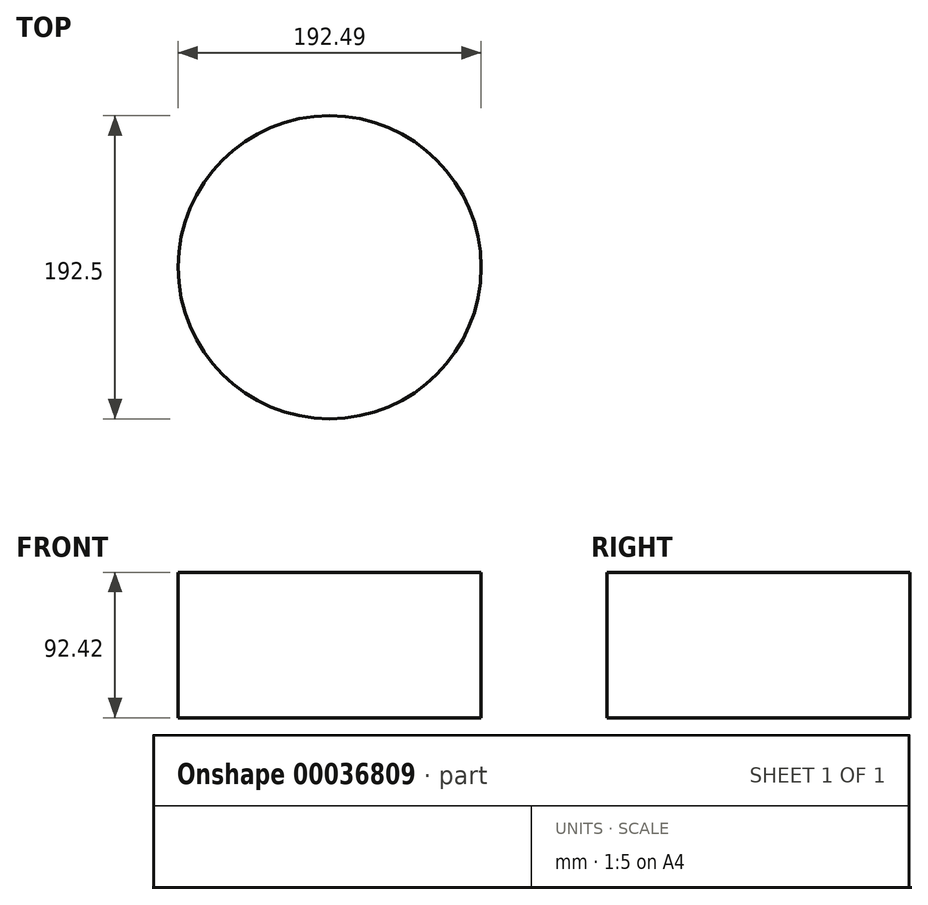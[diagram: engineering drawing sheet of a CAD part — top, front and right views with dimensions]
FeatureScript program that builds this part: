
annotation { "Feature Type Name" : "Feature", "Feature Type Description" : "" }
export const myFeature = defineFeature(function(context is Context, id is Id, definition is map)
    precondition{}
    {
        {
            var Q0;
            Q0=qCreatedBy(makeId("Top.planeOp"),FACE);
            var sketch = newSketch(context, id + "F0", { "sketchPlane" : qUnion([Q0])});
            skCircle(sketch, "E0", {"center": v(22.5, -47.04) * mm, "radius": 96.25 * mm});
            skSolve(sketch);
        }
        {
            var Q0;
            Q0=makeQuery(id+"F0.imprint","IMPRINT",FACE,{"disambiguationData":[TD([[makeQuery(id+"F0.imprint","IMPRINT",EDGE,{"derivedFrom":sQuery(id+"F0.wireOp",EDGE,"E0")}),1.0]])]});
            extrude(context, id + "F1", {"entities" : qUnion([Q0]), "depth" : 92.42 * mm});
        }
    });
